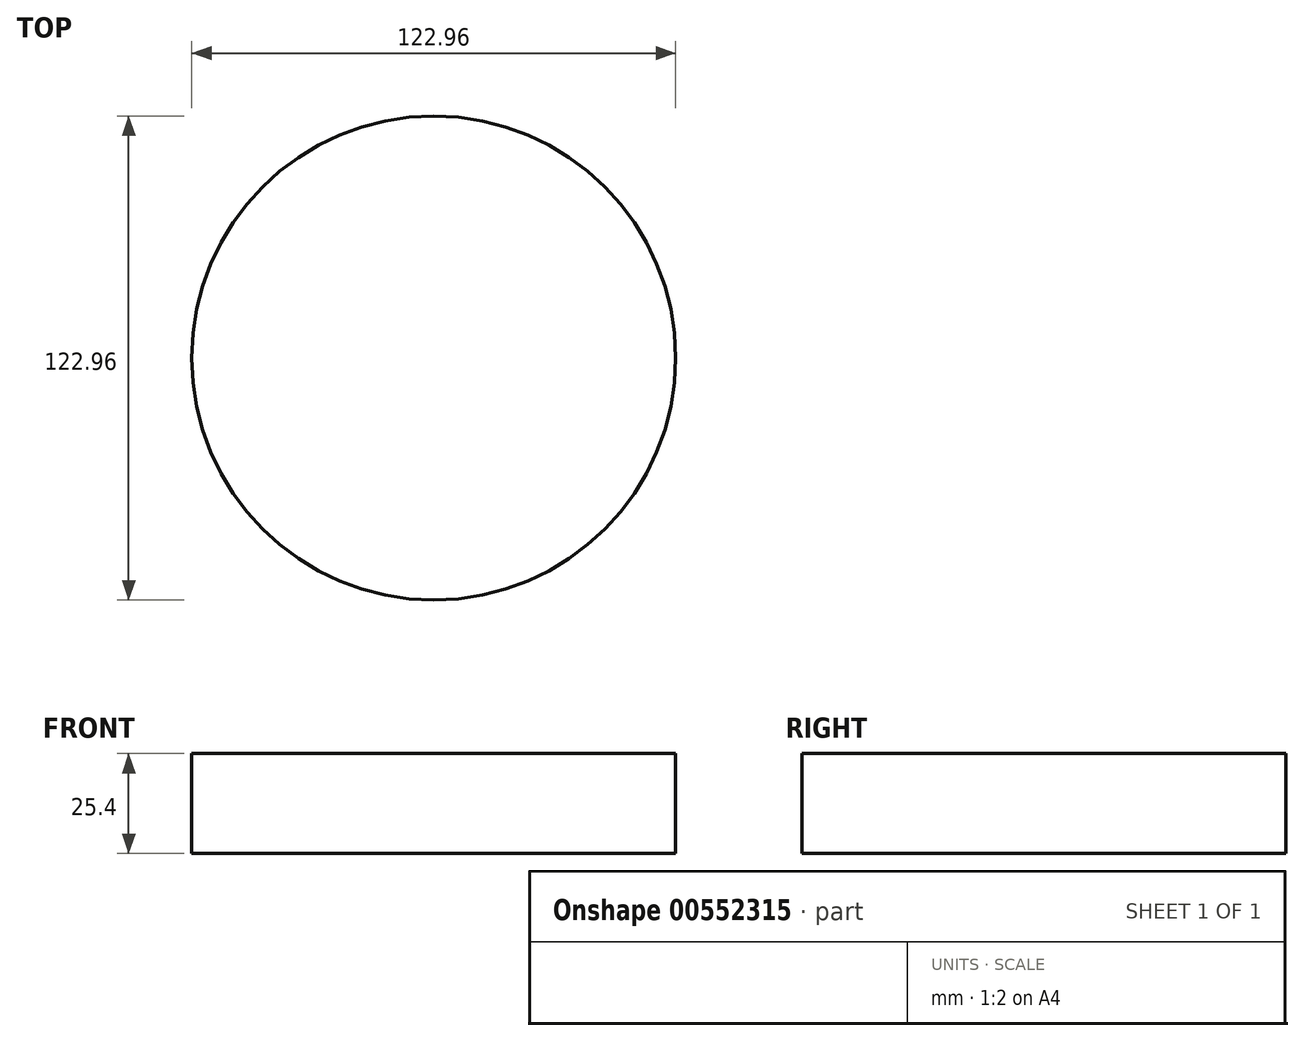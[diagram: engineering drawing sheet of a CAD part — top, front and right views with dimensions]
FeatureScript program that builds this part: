
annotation { "Feature Type Name" : "Feature", "Feature Type Description" : "" }
export const myFeature = defineFeature(function(context is Context, id is Id, definition is map)
    precondition{}
    {
        {
            var Q0;
            Q0=qCreatedBy(makeId("Top.planeOp"),FACE);
            var sketch = newSketch(context, id + "F0", { "sketchPlane" : qUnion([Q0])});
            skCircle(sketch, "E0", {"center": v(0, 0) * mm, "radius": 61.48 * mm});
            skSolve(sketch);
        }
        {
            var Q0;
            Q0=sQuery(id+"F0.wireOp",EDGE,"E0");
            extrude(context, id + "F1", {"bodyType" : ToolBodyType.SURFACE, "surfaceEntities" : qUnion([Q0]), "depth" : 25.4 * mm, "offsetDistance" : 25.4 * mm});
        }
    });
